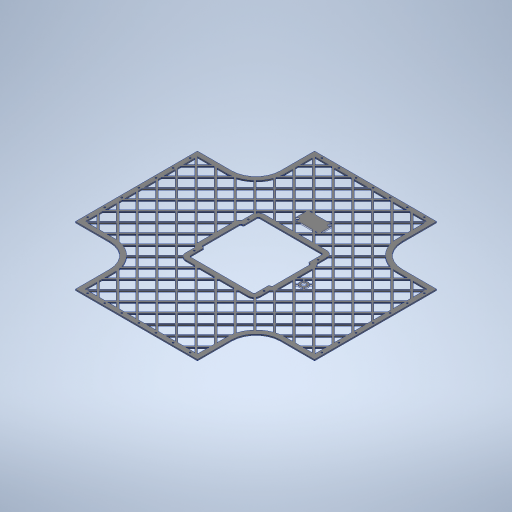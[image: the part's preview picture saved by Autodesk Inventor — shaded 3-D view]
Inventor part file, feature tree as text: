
AUTODESK INVENTOR PART (.ipt)
format: ipt  version: 2024.2 (Build 282272000, 272)  size: 3,692,032 bytes
history: native  units: in
note: dims shown in document units (in); Inventor stores cm internally (conversion verified against a paired STEP export)
features: projected_geometry x82, extrude x11, sketch x11
ambient origin geometry x8: Origin, YZ Plane, XZ Plane, XY Plane, X Axis, Y Axis, Z Axis, Center Point
bodies: Body1 (feature_tree)
feature tree (104):
  extrude  "Extrusion5"  Depth=24.5in
  extrude  "Extrusion6"  Depth=0.5in
  extrude  "Extrusion8"  Depth=1.5748in
  extrude  "Extrusion9"  Depth=1.5748in
  extrude  "Extrusion13"  Depth=2.5in
  extrude  "Extrusion14"  Depth=0.5in
  extrude  "Extrusion15"  TaperAngle=45.0deg  [1 undecoded]
  extrude  "Extrusion16"  Depth=1.42in
  extrude  "Extrusion17"  TaperAngle=135.0deg  [1 undecoded]
  extrude  "Extrusion19"  Depth=0.2in TaperAngle=0.0deg
  extrude  "Extrusion20"  Depth=7.063in
  sketch  "Sketch6"  dims[d60=24.5in d61=24.5in]
  sketch  "Sketch7"  dims[d62=0.125in d63=0.0in d64=0.5in]
  projected_geometry  "Projected Loop2"
  sketch  "Sketch8"  dims[d65=0.157in d66=1.5748in d68=1.75in d69=1.5748in d71=1.75in]
  projected_geometry  "Projected Loop3"
  sketch  "Sketch9"  dims[d74=0.157in d75=1.5748in d77=1.75in d78=1.5748in d80=1.75in]
  projected_geometry  "Projected Loop4"
  sketch  "Sketch12"  dims[d83=0.125in d84=0.0in d93=2.5in]
  projected_geometry  "Projected Loop5"
  sketch  "Sketch13"  dims[d94=2.4375in d95=0.0in d96=0.5in]
  sketch  "Sketch14"  dims[d97=1.0in d98=45.0deg]
  projected_geometry  "Projected Loop6"
  projected_geometry  "Projected Loop7"
  projected_geometry  "Projected Loop8"
  projected_geometry  "Projected Loop9"
  projected_geometry  "Projected Loop10"
  projected_geometry  "Projected Loop11"
  projected_geometry  "Projected Loop12"
  projected_geometry  "Projected Loop13"
  projected_geometry  "Projected Loop14"
  projected_geometry  "Projected Loop15"
  projected_geometry  "Projected Loop16"
  projected_geometry  "Projected Loop17"
  projected_geometry  "Projected Loop18"
  projected_geometry  "Projected Loop19"
  projected_geometry  "Projected Loop20"
  projected_geometry  "Projected Loop21"
  projected_geometry  "Projected Loop22"
  projected_geometry  "Projected Loop23"
  projected_geometry  "Projected Loop24"
  projected_geometry  "Projected Loop25"
  projected_geometry  "Projected Loop26"
  projected_geometry  "Projected Loop27"
  projected_geometry  "Projected Loop28"
  projected_geometry  "Projected Loop29"
  projected_geometry  "Projected Loop30"
  projected_geometry  "Projected Loop31"
  projected_geometry  "Projected Loop32"
  projected_geometry  "Projected Loop33"
  projected_geometry  "Projected Loop34"
  projected_geometry  "Projected Loop35"
  projected_geometry  "Projected Loop36"
  projected_geometry  "Projected Loop37"
  projected_geometry  "Projected Loop38"
  projected_geometry  "Projected Loop39"
  projected_geometry  "Projected Loop40"
  projected_geometry  "Projected Loop41"
  projected_geometry  "Projected Loop42"
  projected_geometry  "Projected Loop43"
  projected_geometry  "Projected Loop44"
  projected_geometry  "Projected Loop45"
  projected_geometry  "Projected Loop46"
  projected_geometry  "Projected Loop47"
  projected_geometry  "Projected Loop48"
  projected_geometry  "Projected Loop49"
  projected_geometry  "Projected Loop50"
  projected_geometry  "Projected Loop51"
  projected_geometry  "Projected Loop52"
  projected_geometry  "Projected Loop53"
  projected_geometry  "Projected Loop54"
  projected_geometry  "Projected Loop55"
  projected_geometry  "Projected Loop56"
  projected_geometry  "Projected Loop57"
  projected_geometry  "Projected Loop58"
  projected_geometry  "Projected Loop59"
  projected_geometry  "Projected Loop60"
  projected_geometry  "Projected Loop61"
  projected_geometry  "Projected Loop62"
  projected_geometry  "Projected Loop63"
  projected_geometry  "Projected Loop64"
  projected_geometry  "Projected Loop65"
  projected_geometry  "Projected Loop66"
  projected_geometry  "Projected Loop67"
  projected_geometry  "Projected Loop68"
  projected_geometry  "Projected Loop69"
  projected_geometry  "Projected Loop70"
  projected_geometry  "Projected Loop71"
  projected_geometry  "Projected Loop72"
  projected_geometry  "Projected Loop73"
  projected_geometry  "Projected Loop74"
  projected_geometry  "Projected Loop75"
  projected_geometry  "Projected Loop76"
  projected_geometry  "Projected Loop77"
  projected_geometry  "Projected Loop78"
  projected_geometry  "Projected Loop79"
  projected_geometry  "Projected Loop80"
  projected_geometry  "Projected Loop81"
  projected_geometry  "Projected Loop82"
  projected_geometry  "Projected Loop83"
  sketch  "Sketch15"  dims[d99=0.2in d100=7.4803in d102=1.42in d103=0.3937in d105=1.0in]
  sketch  "Sketch17"  dims[d107=45.0deg d108=135.0deg]
  sketch  "Sketch19"  dims[d109=135.0deg d110=0.2in d111=0.0in]
  sketch  "Sketch20"  dims[d116=6.643in d117=7.063in d120=0.125in d121=0.125in d122=0.125in d123=2.875in d124=0.0in d125=0.125in d126=3.1875in d127=0.0in d128=0.264in d129=0.264in d130=0.264in d131=0.264in d132=0.264in d133=0.371in d134=0.371in d135=0.371in d136=0.371in d137=0.371in d138=0.371in d139=0.371in d140=0.371in d141=0.371in d142=0.371in d144=0.371in d145=3.1875in d146=0.0in d147=1.0in d148=0.0in d149=0.157in d150=0.157in d151=2.1875in d152=0.0in d155=0.443in d156=0.2in d165=2.1875in d166=0.0in d167=2.23in d168=1.05in d170=0.1875in d171=0.0in d172=0.257in d173=0.257in]
note: 2 required parameter values undecoded (feature->parameter linkage not recoverable at this tier; creation-order binding heuristic only, values carry confidence <= 0.55)
